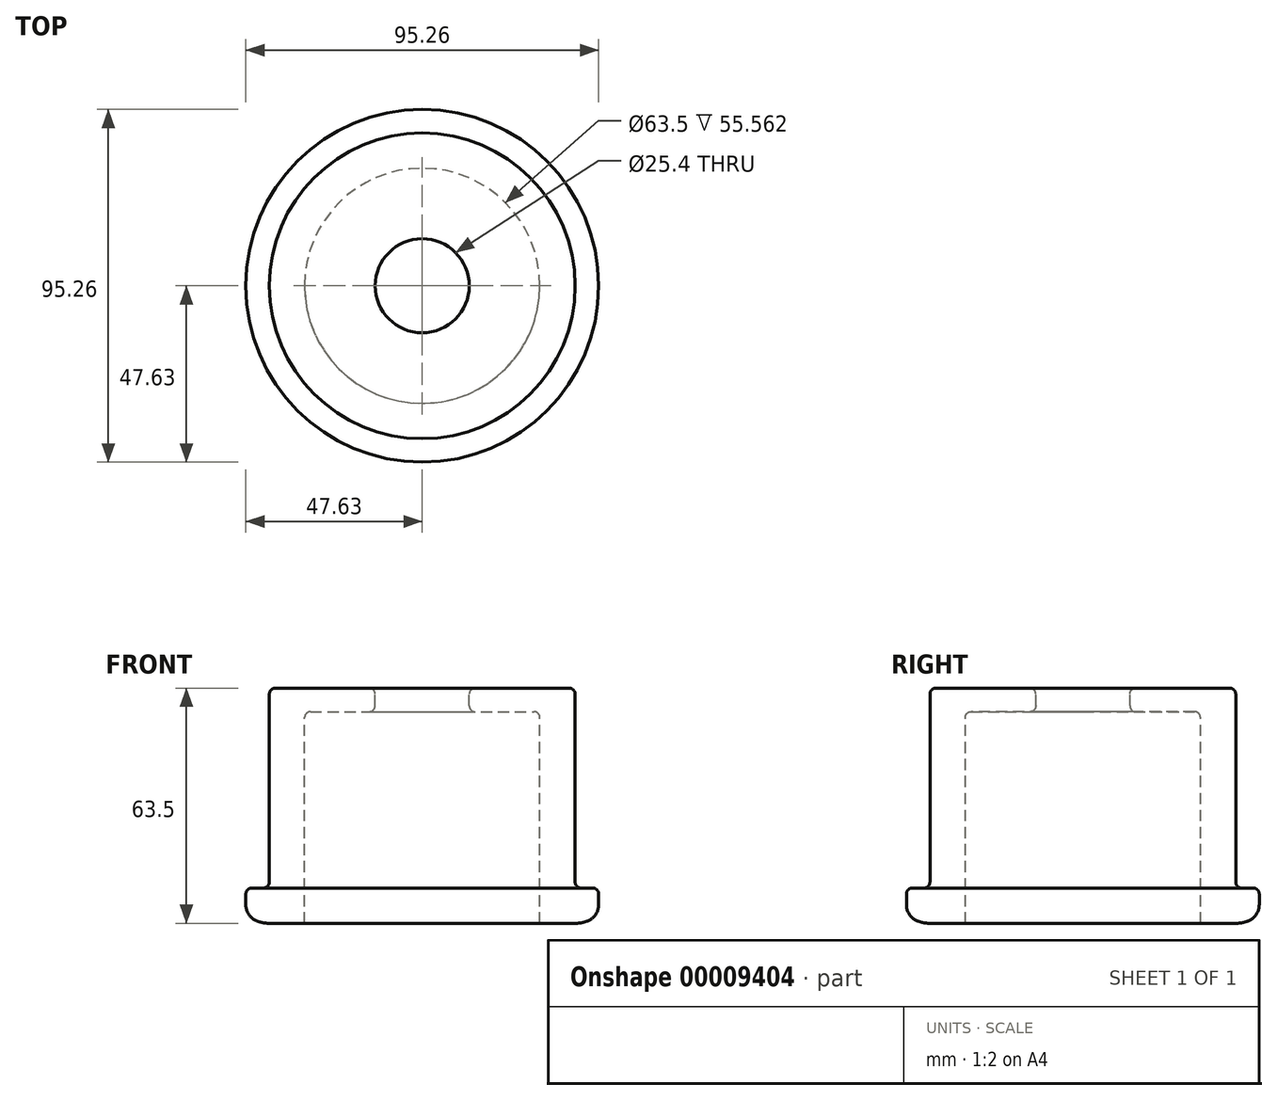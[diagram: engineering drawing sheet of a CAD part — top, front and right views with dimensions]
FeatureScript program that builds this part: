
annotation { "Feature Type Name" : "Feature", "Feature Type Description" : "" }
export const myFeature = defineFeature(function(context is Context, id is Id, definition is map)
    precondition{}
    {
        {
            var Q0;
            Q0=qCreatedBy(makeId("Right.planeOp"),FACE);
            var sketch = newSketch(context, id + "F0", { "sketchPlane" : qUnion([Q0])});
            skLineSegment(sketch, "E0", {"start": v(0, 63.5) * mm, "end": v(0, 0) * mm});
            skLineSegment(sketch, "E1.left", {"start": v(-31.75, 57.15) * mm, "end": v(-31.75, 0) * mm});
            skLineSegment(sketch, "E1.right", {"start": v(-41.28, 63.5) * mm, "end": v(-41.27, 9.53) * mm});
            skLineSegment(sketch, "E2", {"start": v(-41.27, 9.53) * mm, "end": v(-47.63, 9.53) * mm});
            skLineSegment(sketch, "E3", {"start": v(-47.63, 9.53) * mm, "end": v(-47.63, 2.43) * mm});
            skLineSegment(sketch, "E4", {"start": v(-47.62, 0) * mm, "end": v(-41.27, 0) * mm, "construction": true});
            skLineSegment(sketch, "E5", {"start": v(-31.75, 57.15) * mm, "end": v(-12.7, 57.15) * mm});
            skLineSegment(sketch, "E6", {"start": v(-12.7, 57.15) * mm, "end": v(-12.7, 63.5) * mm});
            skLineSegment(sketch, "E7", {"start": v(-12.7, 63.5) * mm, "end": v(-41.28, 63.5) * mm});
            skArc(sketch, "E8", {"start": v(-47.63, 2.43) * mm, "mid": v(-44.67, 0.63) * mm, "end": v(-41.27, 0) * mm});
            skLineSegment(sketch, "E9", {"start": v(-47.63, 2.43) * mm, "end": v(-47.63, 0) * mm, "construction": true});
            skLineSegment(sketch, "E10", {"start": v(-41.27, 0) * mm, "end": v(-31.75, 0) * mm});
            skSolve(sketch);
        }
        {
            var Q0;
            Q0=makeQuery(id+"F0.imprint","IMPRINT",FACE,{"disambiguationData":[TD([[makeQuery(id+"F0.imprint","IMPRINT",EDGE,{"derivedFrom":sQuery(id+"F0.wireOp",EDGE,"E1.left")}),-1.0]])]});
            var Q1;
            Q1=sQuery(id+"F0.wireOp",EDGE,"E0");
            revolve(context, id + "F1", {"entities" : qUnion([Q0]), "axis" : qUnion([Q1]), "revolveType" : RevolveType.FULL});
        }
        {
            var Q0;
            Q0=makeQuery(id+"F1.opRevolve","SWEPT_EDGE",EDGE,{"disambiguationData":[OSD([sQuery(id+"F0.wireOp",EDGE,"E1.right"),sQuery(id+"F0.wireOp",EDGE,"E2")])]});
            var Q1;
            Q1=makeQuery(id+"F1.opRevolve","SWEPT_EDGE",EDGE,{"disambiguationData":[OSD([sQuery(id+"F0.wireOp",EDGE,"E2"),sQuery(id+"F0.wireOp",EDGE,"E3")])]});
            var Q2;
            Q2=makeQuery(id+"F1.opRevolve","SWEPT_EDGE",EDGE,{"disambiguationData":[OSD([sQuery(id+"F0.wireOp",EDGE,"E1.right"),sQuery(id+"F0.wireOp",EDGE,"E7")])]});
            var Q3;
            Q3=makeQuery(id+"F1.opRevolve","SWEPT_EDGE",EDGE,{"disambiguationData":[OSD([sQuery(id+"F0.wireOp",EDGE,"E1.left"),sQuery(id+"F0.wireOp",EDGE,"E5")])]});
            var Q4;
            Q4=makeQuery(id+"F1.opRevolve","SWEPT_EDGE",EDGE,{"disambiguationData":[OSD([sQuery(id+"F0.wireOp",EDGE,"E5"),sQuery(id+"F0.wireOp",EDGE,"E6")])]});
            var Q5;
            Q5=makeQuery(id+"F1.opRevolve","SWEPT_EDGE",EDGE,{"disambiguationData":[OSD([sQuery(id+"F0.wireOp",EDGE,"E6"),sQuery(id+"F0.wireOp",EDGE,"E7")])]});
            fillet(context, id + "F2", {"entities" : qUnion([Q0, Q1, Q2, Q3, Q4, Q5]), "radius" : 1.59 * mm, "tangentPropagation" : true, "allowEdgeOverflow" : false});
        }
        {
            var Q0;
            Q0=makeQuery(id+"F1.opRevolve","SWEPT_EDGE",EDGE,{"disambiguationData":[OSD([sQuery(id+"F0.wireOp",EDGE,"E3"),sQuery(id+"F0.wireOp",EDGE,"E4")])]});
            fillet(context, id + "F3", {"entities" : qUnion([Q0]), "radius" : 4.76 * mm, "tangentPropagation" : true, "allowEdgeOverflow" : false});
        }
    });
